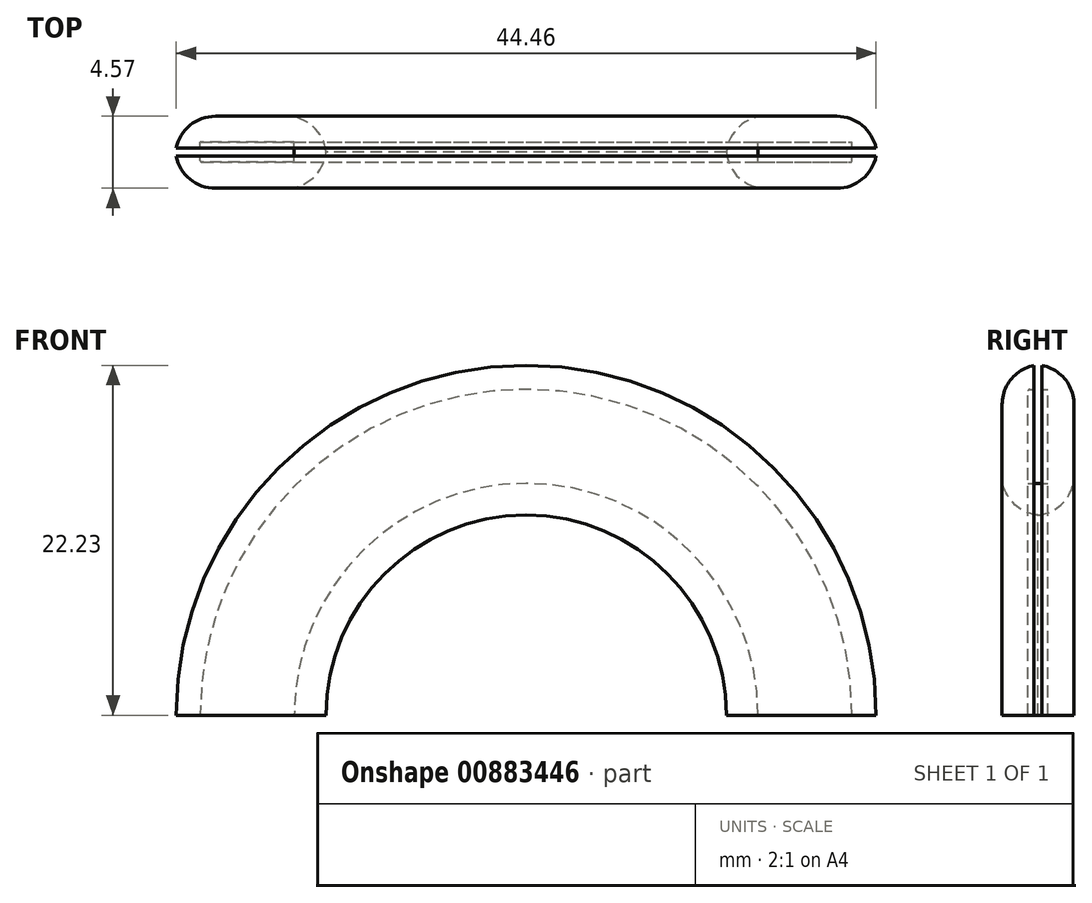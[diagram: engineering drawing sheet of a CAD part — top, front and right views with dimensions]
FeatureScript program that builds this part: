
annotation { "Feature Type Name" : "Feature", "Feature Type Description" : "" }
export const myFeature = defineFeature(function(context is Context, id is Id, definition is map)
    precondition{}
    {
        {
            var Q0;
            Q0=qCreatedBy(makeId("Front.planeOp"),FACE);
            var sketch = newSketch(context, id + "F0", { "sketchPlane" : qUnion([Q0])});
            skArc(sketch, "E0", {"start": v(-12.7, 0) * mm, "mid": v(0, 12.7) * mm, "end": v(12.7, 0) * mm});
            skSolve(sketch);
        }
        {
            var Q0;
            Q0=qCreatedBy(makeId("Top.planeOp"),FACE);
            var sketch = newSketch(context, id + "F1", { "sketchPlane" : qUnion([Q0])});
            skLineSegment(sketch, "E1.bottom", {"start": v(-12.7, 0) * mm, "end": v(-22.23, 0) * mm});
            skLineSegment(sketch, "E1.top", {"start": v(-12.7, -4.57) * mm, "end": v(-22.22, -4.57) * mm});
            skLineSegment(sketch, "E1.left", {"start": v(-12.7, 0) * mm, "end": v(-12.7, -4.57) * mm});
            skLineSegment(sketch, "E1.right", {"start": v(-22.23, 0) * mm, "end": v(-22.23, -2.03) * mm});
            skLineSegment(sketch, "E2.bottom", {"start": v(-22.23, -2.03) * mm, "end": v(-20.7, -2.03) * mm});
            skLineSegment(sketch, "E2.top", {"start": v(-22.23, -2.54) * mm, "end": v(-20.7, -2.54) * mm});
            skLineSegment(sketch, "E3.trimOffspring", {"start": v(-22.23, -2.54) * mm, "end": v(-22.22, -4.57) * mm});
            skLineSegment(sketch, "E4.bottom", {"start": v(-14.73, -2.92) * mm, "end": v(-20.6, -2.92) * mm});
            skLineSegment(sketch, "E4.top", {"start": v(-14.73, -1.65) * mm, "end": v(-20.7, -1.65) * mm});
            skLineSegment(sketch, "E4.left", {"start": v(-14.73, -2.92) * mm, "end": v(-14.73, -1.65) * mm});
            skLineSegment(sketch, "E4.right", {"start": v(-20.7, -2.81) * mm, "end": v(-20.7, -2.54) * mm});
            skLineSegment(sketch, "E5.trimOffspring", {"start": v(-20.7, -2.03) * mm, "end": v(-20.7, -1.65) * mm});
            skPoint(sketch, "E6.orphan", {"position": v(-14.73, -2.54) * mm});
            skPoint(sketch, "E7.visualSharp", {"position": v(-20.7, -2.92) * mm});
            skArc(sketch, "E7.filletArc", {"start": v(-20.7, -2.81) * mm, "mid": v(-20.67, -2.89) * mm, "end": v(-20.6, -2.92) * mm});
            skSolve(sketch);
        }
        {
            var Q0;
            Q0=makeQuery(id+"F1.imprint","IMPRINT",FACE,{"disambiguationData":[TD([[makeQuery(id+"F1.imprint","IMPRINT",EDGE,{"derivedFrom":sQuery(id+"F1.wireOp",EDGE,"E1.bottom")}),1.0]])]});
            var Q1;
            Q1=sQuery(id+"F0.wireOp",EDGE,"E0");
            sweep(context, id + "F2", {"profiles" : qUnion([Q0]), "path" : qUnion([Q1])});
        }
        {
            var Q0;
            Q0=makeQuery(id+"F2.opSweep","SWEPT_EDGE",EDGE,{"disambiguationData":[OSD([sQuery(id+"F0.wireOp",EDGE,"E0"),sQuery(id+"F1.wireOp",EDGE,"E1.top"),sQuery(id+"F1.wireOp",EDGE,"E3.trimOffspring")])]});
            var Q1;
            Q1=makeQuery(id+"F2.opSweep","SWEPT_EDGE",EDGE,{"disambiguationData":[OSD([sQuery(id+"F0.wireOp",EDGE,"E0"),sQuery(id+"F1.wireOp",EDGE,"E1.bottom"),sQuery(id+"F1.wireOp",EDGE,"E1.right")])]});
            var Q2;
            Q2=makeQuery(id+"F2.opSweep","SWEPT_EDGE",EDGE,{"disambiguationData":[OSD([sQuery(id+"F0.wireOp",EDGE,"E0"),sQuery(id+"F1.wireOp",EDGE,"E1.top"),sQuery(id+"F1.wireOp",EDGE,"E1.left")])]});
            var Q3;
            Q3=makeQuery(id+"F2.opSweep","SWEPT_EDGE",EDGE,{"disambiguationData":[OSD([sQuery(id+"F0.wireOp",EDGE,"E0"),sQuery(id+"F1.wireOp",EDGE,"E1.bottom"),sQuery(id+"F1.wireOp",EDGE,"E1.left")])]});
            fillet(context, id + "F3", {"entities" : qUnion([Q0, Q1, Q2, Q3]), "radius" : 2.54 * mm, "tangentPropagation" : true, "allowEdgeOverflow" : false});
        }
    });
